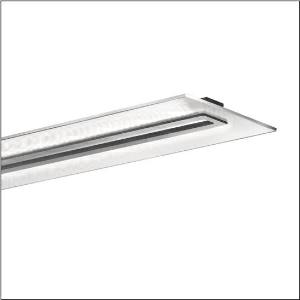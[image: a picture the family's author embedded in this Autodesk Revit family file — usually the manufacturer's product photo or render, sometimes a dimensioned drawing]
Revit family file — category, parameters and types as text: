
# Revit family: vega_r__11_5mn238dle_9bfa
name_source: partatom
category: Lighting Fixtures
units: mm (PartAtom-declared; Revit-internal decimal feet)

## family parameters
Cut with Voids When Loaded = No
Host = Face
Light Source = No
Part Type = Normal
Room Calculation Point = No
Round Connector Dimension = Use Diameter
Shared = No

## types (1)
- --- (1 x LED 4000K / CRI = 80 (unbekannt), 8130 lm, 4000K)
    Apparent Load = 62 VA
    CIE Flux Codes = 61 86 97 62 100
    Color Rendering = 80
    Color Temperature = 4000K
    Default Elevation = 1800 mm
    Description = Vega® 11, office luminaire, primary light control with prismatic reflector, of PMMA, transparent prismatic structure, CAT 2 (L<= 1500cd/m²), light emission: direct/indirect distribution, primary light characteristic: symmetric, installation type: suspended mounting, surface-mounted, LED, rated luminous flux: 8.130lm, luminous efficacy: 131lm/W, light colour: 840, colour temperature: 4000K, control gear: ECG, with terminal, 3+2-pole, max. 2.5mm², mains connection: 230V, AC, 50Hz, connection cable inclusive, cable length: 1,5m, rated input power: 62W, luminaire housing, rectangular, rounded, of aluminium section, anodised, metallic grey (RAL 9006), length: 1.250mm, width: 350mm, height: 43mm, luminaire housing, lower part, of aluminium section, anodised, metallic grey (RAL 9006), of PC, grey, protection rating (complete): IP20, insulation class (complete): insulation class I (protective earthing), certification: CE, standard: EN 50419, packaging unit: 1 piece
    Height = 40 mm  [stored 0.131234 ft]
    Lamp = 1 x LED 4000K / CRI >= 80 (unbekannt)
    Lamp Light Flux = 8130 lm
    Lamp count = 1
    Length = 1250 mm
    Luminous efficacy = 131 lm/W
    Manufacturer = Siteco
    ModVariant = No
    Model = 5MN238DLE
    Mounting Place = Ceiling
    Mounting Type = Pendant
    Number of Poles = 1
    OnlyDefault = Yes
    Power Factor = 1
    Product Name = Vega® 11
    Product group = office luminaire | ceiling pendant
    ProductGroupID = 902
    Protection Class = Protection class I
    Protection Degree = IP 20
    RLX_Detail_Level = 1
    RLX_Emergency_Light_Flux = 0 lm
    RLX_Emergency_Type = 0
    RLX_Emergency_Type_DB = No
    RlxData = <blob elided: 62945 chars, md5=7417e90a>
    Socket = socket
    Standby Power = 0 W
    System Light Flux = 8130 lm
    System Power = 62 W
    Type Comments = factory setting: luminous flux: 100 % | dim-lin: 254 | 458 mA
    Type Image = l_1004807.jpg
    URL = http://relux.com
    VarID = @adj_165661
    Voltage = 0 V
    Weight = 0.00 kg
    Width = 350 mm

note: [stored X ft] marks values corroborated as IEEE doubles in the binary element streams (Revit-internal decimal feet)

## geometry (parser evidence)
native form markers: Blend x4, Sweep x10
no freeform markers — native parametric forms only
